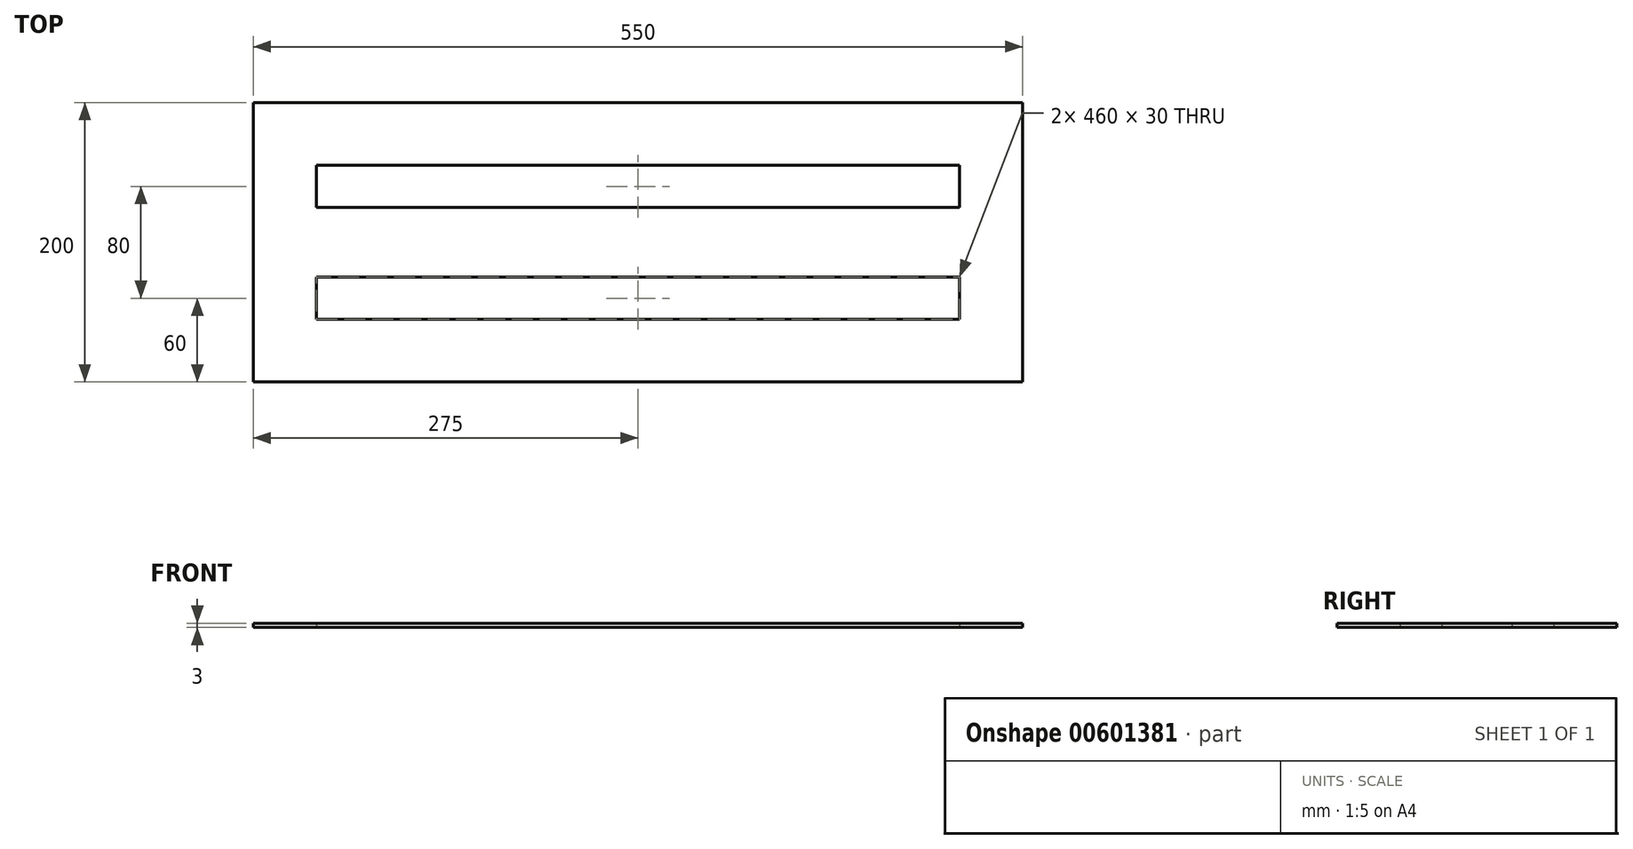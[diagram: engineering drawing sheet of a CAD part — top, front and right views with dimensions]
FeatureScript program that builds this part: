
annotation { "Feature Type Name" : "Feature", "Feature Type Description" : "" }
export const myFeature = defineFeature(function(context is Context, id is Id, definition is map)
    precondition{}
    {
        {
            var Q0;
            Q0=qCreatedBy(makeId("Top.planeOp"),FACE);
            var sketch = newSketch(context, id + "F0", { "sketchPlane" : qUnion([Q0])});
            skLineSegment(sketch, "E0.bottom", {"start": v(275, -100) * mm, "end": v(-275, -100) * mm});
            skLineSegment(sketch, "E0.top", {"start": v(275, 100) * mm, "end": v(-275, 100) * mm});
            skLineSegment(sketch, "E0.left", {"start": v(275, -100) * mm, "end": v(275, 100) * mm});
            skLineSegment(sketch, "E0.right", {"start": v(-275, -100) * mm, "end": v(-275, 100) * mm});
            skPoint(sketch, "E0.middle", {"position": v(0, 0) * mm});
            skLineSegment(sketch, "E1.bottom", {"start": v(230, 25) * mm, "end": v(-230, 25) * mm});
            skLineSegment(sketch, "E1.top", {"start": v(230, 55) * mm, "end": v(-230, 55) * mm});
            skLineSegment(sketch, "E1.left", {"start": v(230, 25) * mm, "end": v(230, 55) * mm});
            skLineSegment(sketch, "E1.right", {"start": v(-230, 25) * mm, "end": v(-230, 55) * mm});
            skPoint(sketch, "E1.middle", {"position": v(0, 40) * mm});
            skLineSegment(sketch, "E2.bottom", {"start": v(230, -55) * mm, "end": v(-230, -55) * mm});
            skLineSegment(sketch, "E2.top", {"start": v(230, -25) * mm, "end": v(-230, -25) * mm});
            skLineSegment(sketch, "E2.left", {"start": v(230, -55) * mm, "end": v(230, -25) * mm});
            skLineSegment(sketch, "E2.right", {"start": v(-230, -55) * mm, "end": v(-230, -25) * mm});
            skPoint(sketch, "E2.middle", {"position": v(0, -40) * mm});
            skSolve(sketch);
        }
        {
            var Q0;
            Q0=qSketchRegion(id+"F0",true);
            extrude(context, id + "F1", {"entities" : qUnion([Q0]), "depth" : 3 * mm, "offsetDistance" : 25 * mm});
        }
    });
